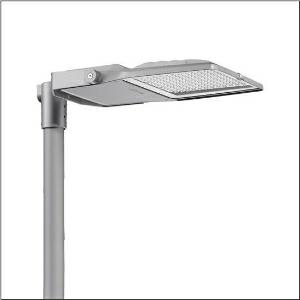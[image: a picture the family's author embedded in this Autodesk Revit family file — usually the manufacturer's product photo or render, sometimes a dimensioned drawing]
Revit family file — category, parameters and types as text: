
# Revit family: floodlight_fl_21_midi___pl33t_5xa7785f2f3a_cf02
name_source: partatom
category: Lighting Fixtures
units: mm (PartAtom-declared; Revit-internal decimal feet)

## family parameters
Cut with Voids When Loaded = No
Host = Face
Light Source = No
Part Type = Normal
Room Calculation Point = No
Round Connector Dimension = Use Diameter
Shared = No

## types (1)
- --- (1 x LED, 35340 lm, 271.6 W, 3000K)
    Apparent Load = 272 VA
    CIE Flux Codes = 26 75 99 100 100
    Color Rendering = 70
    Color Temperature = 3000K
    Default Elevation = 1800 mm
    Description = Floodlight FL 21 midi, floodlight, primary light control with lens, of PMMA, primary optical cover: protective disc, of toughened safety glass, transparent, light distribution: PL33T, light emission: direct distribution, installation type: surface-mounted, LED, High Power LED, rated luminous flux: 35.340lm, luminous efficacy: 130lm/W, light colour: 730, colour temperature: 3000K, control gear: Smart Interface (Zhaga), control: flexible luminous flux parameterisation, time-dependent luminous flux control, constant luminous flux control, overheat protection, pre-setting: logarithmic dimming characteristic, with terminal, 6-pole, mains connection: 220..240V, AC, 50/60Hz, start of lifetime: 272W, end of service life: 287W, reduction: 123W, luminaire housing, of diecast aluminium, powder-coated, SITECO metallic grey (DB 702S), corrosivity category C5 mid according to DIN EN ISO 12944, suitable for swimming pools, chlorine-resistant, sealing non-destructively replaceable, please order mast flange separately, mast bracket, of steel, galvanised, powder-coated, SITECO metallic grey (DB 702S), Smart Interface above, protection rating (complete): IP66, insulation class (complete): insulation class II (safety insulation), certification: CE, ENEC, VDE, protection symbol: D, impact resistance: IK08, permissible operating ambient temperature: -40..+40°C, permissible operating ambient temperature for outdoor applications: -40..+50°C, standard: DIN EN 12944, LABS conformity tested according to VDMA 24364:2018-05, packaging unit: 1 piece

Light Distribution: PL33T
    Height = 76 mm
    Lamp = 1 x LED
    Lamp Light Flux = 35340 lm
    Lamp Power = 271.6 W
    Lamp count = 1
    Length = 657 mm
    Luminous efficacy = 130 lm/W
    Manufacturer = Siteco
    ModVariant = No
    Model = 5XA7785F2F3A
    Number of Poles = 1
    OnlyDefault = Yes
    Power Factor = 1
    Product Name = Floodlight FL 21 midi | PL33T
    Product group = floodlight | pylon annexe
    ProductGroupID = 6201
    Protection Class = Protection class II
    Protection Degree = IP 66
    RLX_Detail_Level = 1
    RLX_Emergency_Light_Flux = 0 lm
    RLX_Emergency_Type = 0
    RLX_Emergency_Type_DB = No
    RlxData = <blob elided: 153705 chars, md5=14d5bbfd>
    Socket = socket
    Standby Power = 0 W
    System Light Flux = 35340 lm
    System Power = 272 W
    Type Comments = factory setting: luminous flux: 100 % | dim-lin: 254 | 620 mA
    Type Image = l_1007123.jpg
    URL = http://relux.com
    VarID = @adj_149963
    Voltage = 0 V
    Weight = 0.00 kg
    Width = 442 mm

## geometry (parser evidence)
native form markers: Blend x4, Sweep x14
no freeform markers — native parametric forms only
